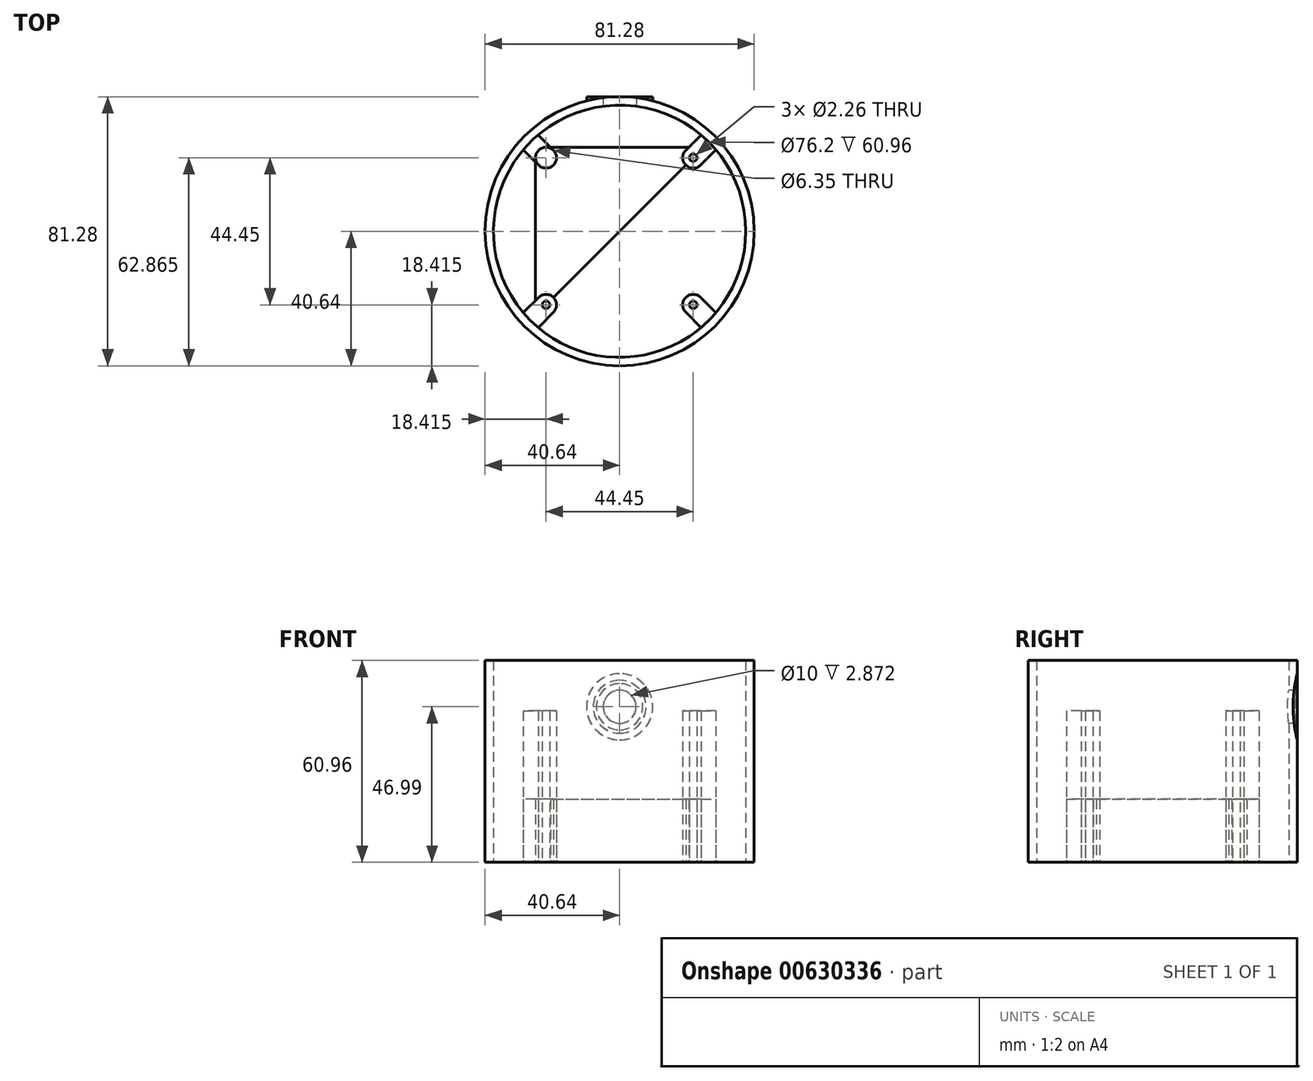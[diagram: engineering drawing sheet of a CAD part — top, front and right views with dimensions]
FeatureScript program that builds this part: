
annotation { "Feature Type Name" : "Feature", "Feature Type Description" : "" }
export const myFeature = defineFeature(function(context is Context, id is Id, definition is map)
    precondition{}
    {
        {
            var Q0;
            Q0=qCreatedBy(makeId("Top.planeOp"),FACE);
            var sketch = newSketch(context, id + "F0", { "sketchPlane" : qUnion([Q0])});
            skLineSegment(sketch, "E0.bottom", {"start": v(-25.4, 25.4) * mm, "end": v(25.4, 25.4) * mm});
            skLineSegment(sketch, "E0.top", {"start": v(-25.4, -25.4) * mm, "end": v(25.4, -25.4) * mm});
            skLineSegment(sketch, "E0.left", {"start": v(-25.4, 25.4) * mm, "end": v(-25.4, -25.4) * mm});
            skLineSegment(sketch, "E0.right", {"start": v(25.4, 25.4) * mm, "end": v(25.4, -25.4) * mm});
            skPoint(sketch, "E0.middle", {"position": v(0, 0) * mm});
            skCircle(sketch, "E1", {"center": v(-22.23, -22.23) * mm, "radius": 1.13 * mm});
            skCircle(sketch, "E2", {"center": v(22.22, 22.23) * mm, "radius": 1.13 * mm});
            skCircle(sketch, "E3", {"center": v(0, 0) * mm, "radius": 38.1 * mm});
            skCircle(sketch, "E4", {"center": v(0, 0) * mm, "radius": 40.64 * mm});
            skLineSegment(sketch, "E5", {"start": v(-25.4, -25.4) * mm, "end": v(25.4, 25.4) * mm});
            skLineSegment(sketch, "E6", {"start": v(-25.4, 25.4) * mm, "end": v(25.4, -25.4) * mm});
            skCircle(sketch, "E7", {"center": v(-22.23, -22.23) * mm, "radius": 3.18 * mm});
            skLineSegment(sketch, "E8", {"start": v(-22.6, -18.12) * mm, "end": v(-33.07, -28.58) * mm});
            skLineSegment(sketch, "E9", {"start": v(-17.1, -21.6) * mm, "end": v(-27.95, -32.44) * mm});
            skCircle(sketch, "E10", {"center": v(22.22, 22.23) * mm, "radius": 3.18 * mm});
            skLineSegment(sketch, "E11", {"start": v(27.08, 31.57) * mm, "end": v(15.84, 20.33) * mm});
            skLineSegment(sketch, "E12", {"start": v(21.85, 17.36) * mm, "end": v(33.43, 28.94) * mm});
            skCircle(sketch, "E13", {"center": v(-22.23, 22.23) * mm, "radius": 1.13 * mm});
            skCircle(sketch, "E14", {"center": v(22.23, -22.23) * mm, "radius": 1.13 * mm});
            skCircle(sketch, "E15", {"center": v(-22.23, 22.23) * mm, "radius": 3.18 * mm});
            skLineSegment(sketch, "E16", {"start": v(-24.44, 19.95) * mm, "end": v(-31.62, 27.13) * mm});
            skLineSegment(sketch, "E17", {"start": v(-19.9, 24.4) * mm, "end": v(-27.14, 31.63) * mm});
            skCircle(sketch, "E18", {"center": v(22.23, -22.23) * mm, "radius": 3.18 * mm});
            skLineSegment(sketch, "E19", {"start": v(19.8, -24.28) * mm, "end": v(28.43, -32.92) * mm});
            skLineSegment(sketch, "E20", {"start": v(23.82, -19.33) * mm, "end": v(35.07, -30.58) * mm});
            skSolve(sketch);
        }
        {
            var Q0;
            {var subQ0=sQuery(id+"F0.wireOp",EDGE,"E11");var subQ1=sQuery(id+"F0.wireOp",EDGE,"E3");var subQ2=makeQuery(id+"F0.imprint","INTERSECT",VERTEX,{"derivedFrom":[subQ1,subQ0]});Q0=makeQuery(id+"F0.imprint","IMPRINT",FACE,{"disambiguationData":[TD([[makeQuery(id+"F0.imprint","IMPRINT",EDGE,{"disambiguationData":[TD([[subQ2,-1.0]])],"derivedFrom":subQ1}),-1.0]])]});}
            var Q1;
            {var subQ0=sQuery(id+"F0.wireOp",EDGE,"E8");var subQ1=sQuery(id+"F0.wireOp",EDGE,"E3");var subQ2=makeQuery(id+"F0.imprint","INTERSECT",VERTEX,{"derivedFrom":[subQ1,subQ0]});Q1=makeQuery(id+"F0.imprint","IMPRINT",FACE,{"disambiguationData":[TD([[makeQuery(id+"F0.imprint","IMPRINT",EDGE,{"disambiguationData":[TD([[subQ2,-1.0]])],"derivedFrom":subQ1}),-1.0]])]});}
            var Q2;
            {var subQ0=sQuery(id+"F0.wireOp",EDGE,"E12");var subQ1=sQuery(id+"F0.wireOp",EDGE,"E3");var subQ2=makeQuery(id+"F0.imprint","INTERSECT",VERTEX,{"derivedFrom":[subQ1,subQ0]});Q2=makeQuery(id+"F0.imprint","IMPRINT",FACE,{"disambiguationData":[TD([[makeQuery(id+"F0.imprint","IMPRINT",EDGE,{"disambiguationData":[TD([[subQ2,1.0]])],"derivedFrom":subQ1}),-1.0]])]});}
            var Q3;
            {var subQ0=sQuery(id+"F0.wireOp",EDGE,"E11");var subQ1=sQuery(id+"F0.wireOp",EDGE,"E3");var subQ2=makeQuery(id+"F0.imprint","INTERSECT",VERTEX,{"derivedFrom":[subQ1,subQ0]});Q3=makeQuery(id+"F0.imprint","IMPRINT",FACE,{"disambiguationData":[TD([[makeQuery(id+"F0.imprint","IMPRINT",EDGE,{"disambiguationData":[TD([[subQ2,1.0]])],"derivedFrom":subQ1}),-1.0]])]});}
            var Q4;
            {var subQ0=sQuery(id+"F0.wireOp",EDGE,"E17");var subQ1=sQuery(id+"F0.wireOp",EDGE,"E3");var subQ2=makeQuery(id+"F0.imprint","INTERSECT",VERTEX,{"derivedFrom":[subQ1,subQ0]});Q4=makeQuery(id+"F0.imprint","IMPRINT",FACE,{"disambiguationData":[TD([[makeQuery(id+"F0.imprint","IMPRINT",EDGE,{"disambiguationData":[TD([[subQ2,-1.0]])],"derivedFrom":subQ1}),-1.0]])]});}
            var Q5;
            {var subQ0=sQuery(id+"F0.wireOp",EDGE,"E16");var subQ1=sQuery(id+"F0.wireOp",EDGE,"E3");var subQ2=makeQuery(id+"F0.imprint","INTERSECT",VERTEX,{"derivedFrom":[subQ1,subQ0]});Q5=makeQuery(id+"F0.imprint","IMPRINT",FACE,{"disambiguationData":[TD([[makeQuery(id+"F0.imprint","IMPRINT",EDGE,{"disambiguationData":[TD([[subQ2,-1.0]])],"derivedFrom":subQ1}),-1.0]])]});}
            var Q6;
            {var subQ0=sQuery(id+"F0.wireOp",EDGE,"E9");var subQ1=sQuery(id+"F0.wireOp",EDGE,"E3");var subQ2=makeQuery(id+"F0.imprint","INTERSECT",VERTEX,{"derivedFrom":[subQ1,subQ0]});Q6=makeQuery(id+"F0.imprint","IMPRINT",FACE,{"disambiguationData":[TD([[makeQuery(id+"F0.imprint","IMPRINT",EDGE,{"disambiguationData":[TD([[subQ2,-1.0]])],"derivedFrom":subQ1}),-1.0]])]});}
            var Q7;
            {var subQ0=sQuery(id+"F0.wireOp",EDGE,"E19");var subQ1=sQuery(id+"F0.wireOp",EDGE,"E3");var subQ2=makeQuery(id+"F0.imprint","INTERSECT",VERTEX,{"derivedFrom":[subQ1,subQ0]});Q7=makeQuery(id+"F0.imprint","IMPRINT",FACE,{"disambiguationData":[TD([[makeQuery(id+"F0.imprint","IMPRINT",EDGE,{"disambiguationData":[TD([[subQ2,-1.0]])],"derivedFrom":subQ1}),-1.0]])]});}
            extrude(context, id + "F1", {"entities" : qUnion([Q0, Q1, Q2, Q3, Q4, Q5, Q6, Q7]), "depth" : 60.96 * mm, "offsetDistance" : 25.4 * mm});
        }
        {
            var Q0;
            {var subQ0=sQuery(id+"F0.wireOp",EDGE,"E11");var subQ1=sQuery(id+"F0.wireOp",EDGE,"E0.bottom");var subQ2=makeQuery(id+"F0.imprint","INTERSECT",VERTEX,{"derivedFrom":[subQ1,subQ0]});Q0=makeQuery(id+"F0.imprint","IMPRINT",FACE,{"disambiguationData":[TD([[makeQuery(id+"F0.imprint","IMPRINT",EDGE,{"disambiguationData":[TD([[subQ2,-1.0]])],"derivedFrom":subQ1}),-1.0]])]});}
            var Q1;
            {var subQ0=sQuery(id+"F0.wireOp",EDGE,"E10");var subQ1=sQuery(id+"F0.wireOp",EDGE,"E0.right");var subQ2=makeQuery(id+"F0.imprint","INTERSECT",VERTEX,{"derivedFrom":[subQ1,subQ0]});Q1=makeQuery(id+"F0.imprint","IMPRINT",FACE,{"disambiguationData":[TD([[makeQuery(id+"F0.imprint","IMPRINT",EDGE,{"disambiguationData":[TD([[subQ2,-1.0]])],"derivedFrom":subQ1}),-1.0]])]});}
            var Q2;
            {var subQ5=sQuery(id+"F0.wireOp",EDGE,"E0.bottom");var subQ8=sQuery(id+"F0.wireOp",EDGE,"E11");var subQ9=makeQuery(id+"F0.imprint","INTERSECT",VERTEX,{"derivedFrom":[subQ5,subQ8]});Q2=makeQuery(id+"F0.imprint","IMPRINT",FACE,{"disambiguationData":[TD([[makeQuery(id+"F0.imprint","IMPRINT",EDGE,{"disambiguationData":[TD([[subQ9,-1.0]])],"derivedFrom":subQ5}),1.0]])]});}
            var Q3;
            {var subQ1=sQuery(id+"F0.wireOp",EDGE,"E0.bottom");var subQ3=sQuery(id+"F0.wireOp",EDGE,"E10");var subQ4=makeQuery(id+"F0.imprint","INTERSECT",VERTEX,{"derivedFrom":[subQ1,subQ3]});Q3=makeQuery(id+"F0.imprint","IMPRINT",FACE,{"disambiguationData":[TD([[makeQuery(id+"F0.imprint","IMPRINT",EDGE,{"disambiguationData":[TD([[subQ4,1.0]])],"derivedFrom":subQ3}),-1.0]])]});}
            var Q4;
            {var subQ1=sQuery(id+"F0.wireOp",EDGE,"E0.right");var subQ3=sQuery(id+"F0.wireOp",EDGE,"E10");var subQ4=makeQuery(id+"F0.imprint","INTERSECT",VERTEX,{"derivedFrom":[subQ1,subQ3]});Q4=makeQuery(id+"F0.imprint","IMPRINT",FACE,{"disambiguationData":[TD([[makeQuery(id+"F0.imprint","IMPRINT",EDGE,{"disambiguationData":[TD([[subQ4,-1.0]])],"derivedFrom":subQ3}),-1.0]])]});}
            var Q5;
            {var subQ0=sQuery(id+"F0.wireOp",EDGE,"E5");var subQ1=sQuery(id+"F0.wireOp",EDGE,"E2");var subQ5=makeQuery(id+"F0.imprint","INTERSECT",VERTEX,{"disambiguationData":[OD(0.0)],"derivedFrom":[subQ1,subQ0]});Q5=makeQuery(id+"F0.imprint","IMPRINT",FACE,{"disambiguationData":[TD([[makeQuery(id+"F0.imprint","IMPRINT",EDGE,{"disambiguationData":[TD([[subQ5,1.0]])],"derivedFrom":subQ1}),-1.0]])]});}
            var Q6;
            {var subQ2=sQuery(id+"F0.wireOp",EDGE,"E5");var subQ4=sQuery(id+"F0.wireOp",EDGE,"E2");var subQ5=makeQuery(id+"F0.imprint","INTERSECT",VERTEX,{"disambiguationData":[OD(0.0)],"derivedFrom":[subQ4,subQ2]});Q6=makeQuery(id+"F0.imprint","IMPRINT",FACE,{"disambiguationData":[TD([[makeQuery(id+"F0.imprint","IMPRINT",EDGE,{"disambiguationData":[TD([[subQ5,-1.0]])],"derivedFrom":subQ4}),-1.0]])]});}
            var Q7;
            {var subQ0=sQuery(id+"F0.wireOp",EDGE,"E8");var subQ1=sQuery(id+"F0.wireOp",EDGE,"E0.left");var subQ2=makeQuery(id+"F0.imprint","INTERSECT",VERTEX,{"derivedFrom":[subQ1,subQ0]});Q7=makeQuery(id+"F0.imprint","IMPRINT",FACE,{"disambiguationData":[TD([[makeQuery(id+"F0.imprint","IMPRINT",EDGE,{"disambiguationData":[TD([[subQ2,-1.0]])],"derivedFrom":subQ1}),1.0]])]});}
            var Q8;
            {var subQ0=sQuery(id+"F0.wireOp",EDGE,"E7");var subQ1=sQuery(id+"F0.wireOp",EDGE,"E0.top");var subQ2=makeQuery(id+"F0.imprint","INTERSECT",VERTEX,{"derivedFrom":[subQ1,subQ0]});Q8=makeQuery(id+"F0.imprint","IMPRINT",FACE,{"disambiguationData":[TD([[makeQuery(id+"F0.imprint","IMPRINT",EDGE,{"disambiguationData":[TD([[subQ2,-1.0]])],"derivedFrom":subQ1}),1.0]])]});}
            var Q9;
            {var subQ1=sQuery(id+"F0.wireOp",EDGE,"E0.left");var subQ3=sQuery(id+"F0.wireOp",EDGE,"E7");var subQ4=makeQuery(id+"F0.imprint","INTERSECT",VERTEX,{"derivedFrom":[subQ1,subQ3]});Q9=makeQuery(id+"F0.imprint","IMPRINT",FACE,{"disambiguationData":[TD([[makeQuery(id+"F0.imprint","IMPRINT",EDGE,{"disambiguationData":[TD([[subQ4,-1.0]])],"derivedFrom":subQ3}),-1.0]])]});}
            var Q10;
            {var subQ1=sQuery(id+"F0.wireOp",EDGE,"E0.top");var subQ3=sQuery(id+"F0.wireOp",EDGE,"E7");var subQ4=makeQuery(id+"F0.imprint","INTERSECT",VERTEX,{"derivedFrom":[subQ1,subQ3]});Q10=makeQuery(id+"F0.imprint","IMPRINT",FACE,{"disambiguationData":[TD([[makeQuery(id+"F0.imprint","IMPRINT",EDGE,{"disambiguationData":[TD([[subQ4,1.0]])],"derivedFrom":subQ3}),-1.0]])]});}
            var Q11;
            {var subQ3=sQuery(id+"F0.wireOp",EDGE,"E7");var subQ9=sQuery(id+"F0.wireOp",EDGE,"E0.top");var subQ10=makeQuery(id+"F0.imprint","INTERSECT",VERTEX,{"derivedFrom":[subQ9,subQ3]});Q11=makeQuery(id+"F0.imprint","IMPRINT",FACE,{"disambiguationData":[TD([[makeQuery(id+"F0.imprint","IMPRINT",EDGE,{"disambiguationData":[TD([[subQ10,-1.0]])],"derivedFrom":subQ9}),-1.0]])]});}
            var Q12;
            {var subQ2=sQuery(id+"F0.wireOp",EDGE,"E5");var subQ4=sQuery(id+"F0.wireOp",EDGE,"E1");var subQ7=makeQuery(id+"F0.imprint","INTERSECT",VERTEX,{"disambiguationData":[OD(0.0)],"derivedFrom":[subQ4,subQ2]});Q12=makeQuery(id+"F0.imprint","IMPRINT",FACE,{"disambiguationData":[TD([[makeQuery(id+"F0.imprint","IMPRINT",EDGE,{"disambiguationData":[TD([[subQ7,-1.0]])],"derivedFrom":subQ4}),-1.0]])]});}
            var Q13;
            {var subQ2=sQuery(id+"F0.wireOp",EDGE,"E5");var subQ4=sQuery(id+"F0.wireOp",EDGE,"E1");var subQ5=makeQuery(id+"F0.imprint","INTERSECT",VERTEX,{"disambiguationData":[OD(0.0)],"derivedFrom":[subQ4,subQ2]});Q13=makeQuery(id+"F0.imprint","IMPRINT",FACE,{"disambiguationData":[TD([[makeQuery(id+"F0.imprint","IMPRINT",EDGE,{"disambiguationData":[TD([[subQ5,1.0]])],"derivedFrom":subQ4}),-1.0]])]});}
            extrude(context, id + "F2", {"entities" : qUnion([Q0, Q1, Q2, Q3, Q4, Q5, Q6, Q7, Q8, Q9, Q10, Q11, Q12, Q13]), "operationType" : NewBodyOperationType.ADD, "depth" : 45.72 * mm, "offsetDistance" : 25.4 * mm});
        }
        {
            var Q0;
            {var subQ0=sQuery(id+"F0.wireOp",EDGE,"E15");var subQ1=sQuery(id+"F0.wireOp",EDGE,"E0.bottom");var subQ2=makeQuery(id+"F0.imprint","INTERSECT",VERTEX,{"derivedFrom":[subQ1,subQ0]});Q0=makeQuery(id+"F0.imprint","IMPRINT",FACE,{"disambiguationData":[TD([[makeQuery(id+"F0.imprint","IMPRINT",EDGE,{"disambiguationData":[TD([[subQ2,-1.0]])],"derivedFrom":subQ1}),-1.0]])]});}
            var Q1;
            {var subQ0=sQuery(id+"F0.wireOp",EDGE,"E15");var subQ1=sQuery(id+"F0.wireOp",EDGE,"E0.left");var subQ2=makeQuery(id+"F0.imprint","INTERSECT",VERTEX,{"derivedFrom":[subQ1,subQ0]});Q1=makeQuery(id+"F0.imprint","IMPRINT",FACE,{"disambiguationData":[TD([[makeQuery(id+"F0.imprint","IMPRINT",EDGE,{"disambiguationData":[TD([[subQ2,-1.0]])],"derivedFrom":subQ1}),1.0]])]});}
            var Q2;
            {var subQ1=sQuery(id+"F0.wireOp",EDGE,"E0.bottom");var subQ3=sQuery(id+"F0.wireOp",EDGE,"E15");var subQ4=makeQuery(id+"F0.imprint","INTERSECT",VERTEX,{"derivedFrom":[subQ1,subQ3]});Q2=makeQuery(id+"F0.imprint","IMPRINT",FACE,{"disambiguationData":[TD([[makeQuery(id+"F0.imprint","IMPRINT",EDGE,{"disambiguationData":[TD([[subQ4,-1.0]])],"derivedFrom":subQ3}),-1.0]])]});}
            var Q3;
            {var subQ1=sQuery(id+"F0.wireOp",EDGE,"E0.left");var subQ3=sQuery(id+"F0.wireOp",EDGE,"E15");var subQ4=makeQuery(id+"F0.imprint","INTERSECT",VERTEX,{"derivedFrom":[subQ1,subQ3]});Q3=makeQuery(id+"F0.imprint","IMPRINT",FACE,{"disambiguationData":[TD([[makeQuery(id+"F0.imprint","IMPRINT",EDGE,{"disambiguationData":[TD([[subQ4,1.0]])],"derivedFrom":subQ3}),-1.0]])]});}
            var Q4;
            {var subQ1=sQuery(id+"F0.wireOp",EDGE,"E6");var subQ4=sQuery(id+"F0.wireOp",EDGE,"E15");var subQ8=makeQuery(id+"F0.imprint","INTERSECT",VERTEX,{"disambiguationData":[OD(0.0)],"derivedFrom":[subQ1,subQ4]});Q4=makeQuery(id+"F0.imprint","IMPRINT",FACE,{"disambiguationData":[TD([[makeQuery(id+"F0.imprint","IMPRINT",EDGE,{"disambiguationData":[TD([[subQ8,-1.0]])],"derivedFrom":subQ1}),1.0]])]});}
            var Q5;
            {var subQ0=sQuery(id+"F0.wireOp",EDGE,"E15");var subQ2=sQuery(id+"F0.wireOp",EDGE,"E6");var subQ3=makeQuery(id+"F0.imprint","INTERSECT",VERTEX,{"disambiguationData":[OD(0.0)],"derivedFrom":[subQ2,subQ0]});Q5=makeQuery(id+"F0.imprint","IMPRINT",FACE,{"disambiguationData":[TD([[makeQuery(id+"F0.imprint","IMPRINT",EDGE,{"disambiguationData":[TD([[subQ3,-1.0]])],"derivedFrom":subQ2}),-1.0]])]});}
            var Q6;
            {var subQ0=sQuery(id+"F0.wireOp",EDGE,"E15");var subQ5=sQuery(id+"F0.wireOp",EDGE,"E0.bottom");var subQ7=makeQuery(id+"F0.imprint","INTERSECT",VERTEX,{"derivedFrom":[subQ5,subQ0]});Q6=makeQuery(id+"F0.imprint","IMPRINT",FACE,{"disambiguationData":[TD([[makeQuery(id+"F0.imprint","IMPRINT",EDGE,{"disambiguationData":[TD([[subQ7,-1.0]])],"derivedFrom":subQ5}),1.0]])]});}
            var Q7;
            {var subQ0=sQuery(id+"F0.wireOp",EDGE,"E20");var subQ1=sQuery(id+"F0.wireOp",EDGE,"E0.right");var subQ2=makeQuery(id+"F0.imprint","INTERSECT",VERTEX,{"derivedFrom":[subQ1,subQ0]});Q7=makeQuery(id+"F0.imprint","IMPRINT",FACE,{"disambiguationData":[TD([[makeQuery(id+"F0.imprint","IMPRINT",EDGE,{"disambiguationData":[TD([[subQ2,-1.0]])],"derivedFrom":subQ1}),-1.0]])]});}
            var Q8;
            {var subQ0=sQuery(id+"F0.wireOp",EDGE,"E19");var subQ1=sQuery(id+"F0.wireOp",EDGE,"E0.top");var subQ2=makeQuery(id+"F0.imprint","INTERSECT",VERTEX,{"derivedFrom":[subQ1,subQ0]});Q8=makeQuery(id+"F0.imprint","IMPRINT",FACE,{"disambiguationData":[TD([[makeQuery(id+"F0.imprint","IMPRINT",EDGE,{"disambiguationData":[TD([[subQ2,-1.0]])],"derivedFrom":subQ1}),1.0]])]});}
            var Q9;
            {var subQ1=sQuery(id+"F0.wireOp",EDGE,"E0.right");var subQ3=sQuery(id+"F0.wireOp",EDGE,"E18");var subQ4=makeQuery(id+"F0.imprint","INTERSECT",VERTEX,{"derivedFrom":[subQ1,subQ3]});Q9=makeQuery(id+"F0.imprint","IMPRINT",FACE,{"disambiguationData":[TD([[makeQuery(id+"F0.imprint","IMPRINT",EDGE,{"disambiguationData":[TD([[subQ4,1.0]])],"derivedFrom":subQ3}),-1.0]])]});}
            var Q10;
            {var subQ1=sQuery(id+"F0.wireOp",EDGE,"E0.top");var subQ3=sQuery(id+"F0.wireOp",EDGE,"E18");var subQ4=makeQuery(id+"F0.imprint","INTERSECT",VERTEX,{"derivedFrom":[subQ1,subQ3]});Q10=makeQuery(id+"F0.imprint","IMPRINT",FACE,{"disambiguationData":[TD([[makeQuery(id+"F0.imprint","IMPRINT",EDGE,{"disambiguationData":[TD([[subQ4,-1.0]])],"derivedFrom":subQ3}),-1.0]])]});}
            var Q11;
            {var subQ0=sQuery(id+"F0.wireOp",EDGE,"E18");var subQ3=sQuery(id+"F0.wireOp",EDGE,"E6");var subQ4=makeQuery(id+"F0.imprint","INTERSECT",VERTEX,{"disambiguationData":[OD(0.0)],"derivedFrom":[subQ3,subQ0]});Q11=makeQuery(id+"F0.imprint","IMPRINT",FACE,{"disambiguationData":[TD([[makeQuery(id+"F0.imprint","IMPRINT",EDGE,{"disambiguationData":[TD([[subQ4,-1.0]])],"derivedFrom":subQ3}),1.0]])]});}
            var Q12;
            {var subQ0=sQuery(id+"F0.wireOp",EDGE,"E18");var subQ2=sQuery(id+"F0.wireOp",EDGE,"E6");var subQ3=makeQuery(id+"F0.imprint","INTERSECT",VERTEX,{"disambiguationData":[OD(0.0)],"derivedFrom":[subQ2,subQ0]});Q12=makeQuery(id+"F0.imprint","IMPRINT",FACE,{"disambiguationData":[TD([[makeQuery(id+"F0.imprint","IMPRINT",EDGE,{"disambiguationData":[TD([[subQ3,-1.0]])],"derivedFrom":subQ2}),-1.0]])]});}
            var Q13;
            {var subQ1=sQuery(id+"F0.wireOp",EDGE,"E0.top");var subQ5=sQuery(id+"F0.wireOp",EDGE,"E19");var subQ6=makeQuery(id+"F0.imprint","INTERSECT",VERTEX,{"derivedFrom":[subQ1,subQ5]});Q13=makeQuery(id+"F0.imprint","IMPRINT",FACE,{"disambiguationData":[TD([[makeQuery(id+"F0.imprint","IMPRINT",EDGE,{"disambiguationData":[TD([[subQ6,-1.0]])],"derivedFrom":subQ1}),-1.0]])]});}
            extrude(context, id + "F3", {"entities" : qUnion([Q0, Q1, Q2, Q3, Q4, Q5, Q6, Q7, Q8, Q9, Q10, Q11, Q12, Q13]), "operationType" : NewBodyOperationType.ADD, "depth" : 19.05 * mm, "offsetDistance" : 25.4 * mm});
        }
        {
            var Q0;
            Q0=qCreatedBy(makeId("Front.planeOp"),FACE);
            var sketch = newSketch(context, id + "F4", { "sketchPlane" : qUnion([Q0])});
            skCircle(sketch, "E21", {"center": v(0, 47) * mm, "radius": 5 * mm});
            skCircle(sketch, "E22", {"center": v(0, 47) * mm, "radius": 7 * mm});
            skCircle(sketch, "E23", {"center": v(0, 47) * mm, "radius": 8 * mm});
            skCircle(sketch, "E24", {"center": v(0, 47) * mm, "radius": 10 * mm});
            skSolve(sketch);
        }
        {
            var Q0;
            Q0=makeQuery(id+"F4.imprint","IMPRINT",FACE,{"disambiguationData":[TD([[makeQuery(id+"F4.imprint","IMPRINT",EDGE,{"derivedFrom":sQuery(id+"F4.wireOp",EDGE,"E21")}),1.0]])]});
            extrude(context, id + "F5", {"entities" : qUnion([Q0]), "operationType" : NewBodyOperationType.REMOVE, "oppositeDirection" : true, "depth" : 254 * mm, "offsetDistance" : 25.4 * mm});
        }
        {
            var Q0;
            Q0=makeQuery(id+"F4.imprint","IMPRINT",FACE,{"disambiguationData":[TD([[makeQuery(id+"F4.imprint","IMPRINT",EDGE,{"derivedFrom":sQuery(id+"F4.wireOp",EDGE,"E21")}),-1.0]])]});
            var Q1;
            Q1=makeQuery(id+"F4.imprint","IMPRINT",FACE,{"disambiguationData":[TD([[makeQuery(id+"F4.imprint","IMPRINT",EDGE,{"derivedFrom":sQuery(id+"F4.wireOp",EDGE,"E23")}),-1.0]])]});
            extrude(context, id + "F6", {"entities" : qUnion([Q0, Q1]), "operationType" : NewBodyOperationType.ADD, "oppositeDirection" : true, "depth" : 40.64 * mm, "offsetDistance" : 25.4 * mm, "hasSecondDirection" : true, "secondDirectionOppositeDirection" : true, "secondDirectionDepth" : 38.1 * mm});
        }
    });
